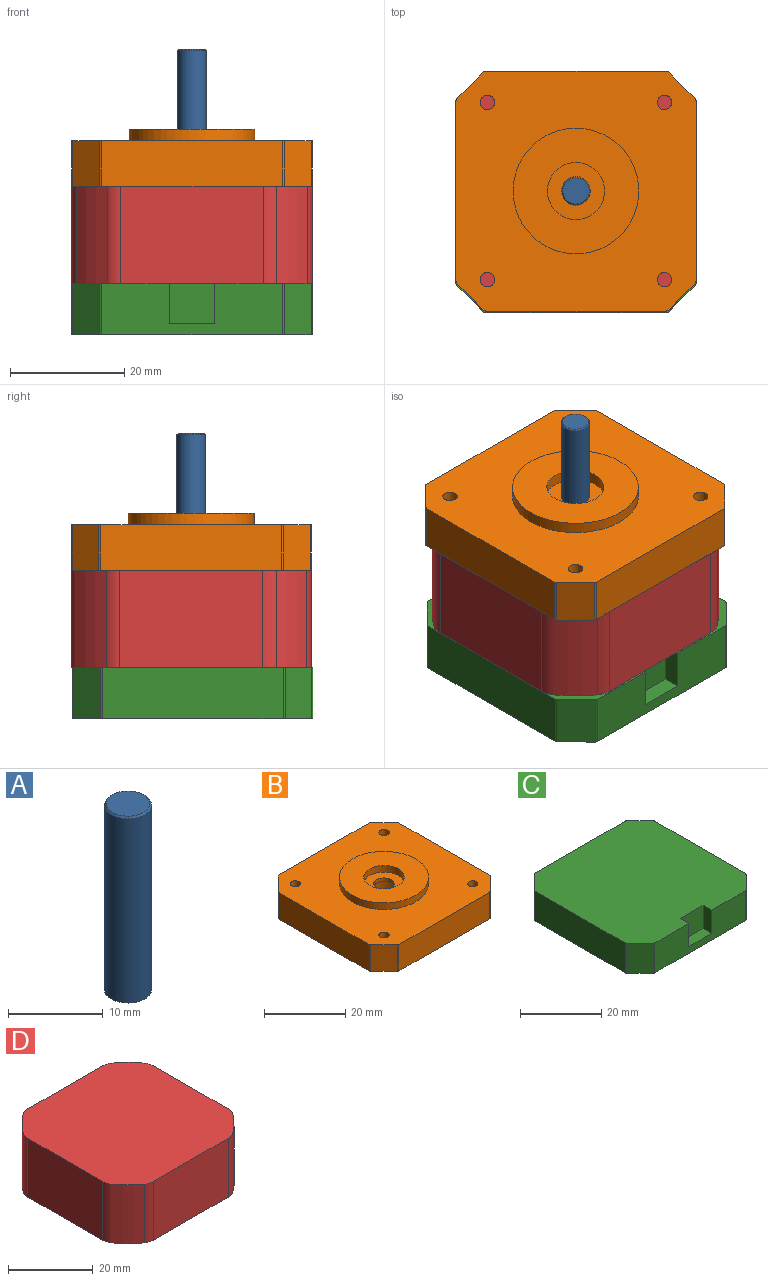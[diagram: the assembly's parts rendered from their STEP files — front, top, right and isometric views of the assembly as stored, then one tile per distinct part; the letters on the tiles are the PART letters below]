
ASSEMBLY  parts=4 mates=3
PART A: 4 faces, bbox 5x5x24 mm
  f0: cone r=2.4mm half-angle=45deg, axis (0,0,-1), area 4.3mm2, adj f1,f2
  f1: cylinder r=2.5mm len=23.8mm, axis (0,0,1), area 373.8mm2, adj f0,f3
  f2: plane 4.6x4.6mm, normal (0,0,1), area 16.6mm2, adj f0
  f3: plane 5x5mm, normal (0,0,-1), area 19.6mm2, adj f1
PART B: 29 faces, bbox 42x42x10 mm
  f0: cylinder r=0.5mm len=8mm, axis (0,0,-1), area 3.1mm2, adj f1,f2,f22,f25
  f1: plane 42x42mm, normal (0,0,1), area 1313.7mm2, adj f0,f2,f3,f4,f5,f6,f7,f8
  f2: plane 8x4.71mm, normal (-0.71,0.71,0), area 53.3mm2, adj f0,f1,f3,f25
  f3: cylinder r=0.5mm len=8mm, axis (0,0,-1), area 3.1mm2, adj f1,f2,f23,f25
  f4: cylinder r=0.5mm len=8mm, axis (0,0,-1), area 3.1mm2, adj f1,f5,f23,f25
  f5: plane 8x4.71mm, normal (-0.71,-0.71,0), area 53.3mm2, adj f1,f4,f6,f25
  f6: cylinder r=0.5mm len=8mm, axis (0,0,-1), area 3.1mm2, adj f1,f5,f24,f25
  f7: cylinder r=0.5mm len=8mm, axis (0,0,-1), area 3.1mm2, adj f1,f8,f24,f25
  f8: plane 8x4.71mm, normal (0.71,-0.71,0), area 53.3mm2, adj f1,f7,f9,f25
  f9: cylinder r=0.5mm len=8mm, axis (0,0,-1), area 3.1mm2, adj f1,f8,f21,f25
  f10: cylinder r=0.5mm len=8mm, axis (0,0,-1), area 3.1mm2, adj f1,f11,f21,f25
  f11: plane 8x4.71mm, normal (0.71,0.71,0), area 53.3mm2, adj f1,f10,f12,f25
  f12: cylinder r=0.5mm len=8mm, axis (0,0,-1), area 3.1mm2, adj f1,f11,f22,f25
  f13: cylinder r=2.5mm len=5mm, axis (0,0,-1), area 15.7mm2, adj f14,f15
  f14: plane 10x10mm, normal (0,0,1), area 58.9mm2, adj f13,f26
  f15: plane 10x10mm, normal (0,0,-1), area 58.9mm2, adj f13,f16
  f16: cylinder r=5mm len=10mm, axis (0,0,1), area 219.9mm2, adj f15,f25
  f17: cylinder r=1.26mm len=8mm, axis (0,0,-1), area 63.6mm2, adj f1,f25
  f18: cylinder r=1.26mm len=8mm, axis (0,0,-1), area 63.6mm2, adj f1,f25
  f19: cylinder r=1.26mm len=8mm, axis (0,0,-1), area 63.6mm2, adj f1,f25
  f20: cylinder r=1.26mm len=8mm, axis (0,0,-1), area 63.6mm2, adj f1,f25
  f21: plane 31.59x8mm, normal (1,0,0), area 252.7mm2, adj f1,f9,f10,f25
  f22: plane 31.59x8mm, normal (0,1,0), area 252.7mm2, adj f0,f1,f12,f25
  f23: plane 31.59x8mm, normal (-1,0,0), area 252.7mm2, adj f1,f3,f4,f25
  f24: plane 31.59x8mm, normal (0,-1,0), area 252.7mm2, adj f1,f6,f7,f25
  f25: plane 42x42mm, normal (0,0,-1), area 1615.3mm2, adj f0,f2,f3,f4,f5,f6,f7,f8
  f26: cylinder r=5mm len=10mm, axis (0,0,1), area 62.8mm2, adj f14,f28
  f27: cylinder r=11mm len=22mm, axis (0,0,1), area 138.2mm2, adj f1,f28
  f28: plane 22x22mm, normal (0,0,1), area 301.6mm2, adj f26,f27
PART C: 32 faces, bbox 42x42x9 mm
  f0: plane 7x3mm, normal (-1,0,0), area 21mm2, adj f2,f3,f4,f29
  f1: plane 7x3mm, normal (1,0,0), area 21mm2, adj f2,f3,f4,f29
  f2: plane 8x3mm, normal (0,0,1), area 24mm2, adj f0,f1,f3,f29
  f3: plane 8x7mm, normal (0,-1,0), area 56mm2, adj f0,f1,f2,f4
  f4: plane 42x42mm, normal (0,0,1), area 1690mm2, adj f0,f1,f3,f5,f7,f8,f9,f10
  f5: cylinder r=0.5mm len=9mm, axis (0,0,1), area 3.5mm2, adj f4,f6,f7,f30
  f6: plane 42x42mm, normal (0,0,-1), area 1530mm2, adj f5,f7,f8,f9,f10,f11,f12,f13
  f7: plane 9x4.71mm, normal (-0.71,0.71,0), area 59.9mm2, adj f4,f5,f6,f8
  f8: cylinder r=0.5mm len=9mm, axis (0,0,1), area 3.5mm2, adj f4,f6,f7,f31
  f9: cylinder r=0.5mm len=9mm, axis (0,0,1), area 3.5mm2, adj f4,f6,f10,f29
  f10: plane 9x4.71mm, normal (-0.71,-0.71,0), area 59.9mm2, adj f4,f6,f9,f11
  f11: cylinder r=0.5mm len=9mm, axis (0,0,1), area 3.5mm2, adj f4,f6,f10,f30
  f12: cylinder r=0.5mm len=9mm, axis (0,0,1), area 3.5mm2, adj f4,f6,f13,f29
  f13: plane 9x4.71mm, normal (0.71,-0.71,0), area 59.9mm2, adj f4,f6,f12,f14
  f14: cylinder r=0.5mm len=9mm, axis (0,0,1), area 3.5mm2, adj f4,f6,f13,f15
  f15: plane 31.59x9mm, normal (1,0,0), area 284.3mm2, adj f4,f6,f14,f16
  f16: cylinder r=0.5mm len=9mm, axis (0,0,1), area 3.5mm2, adj f4,f6,f15,f17
  f17: plane 9x4.71mm, normal (0.71,0.71,0), area 59.9mm2, adj f4,f6,f16,f18
  f18: cylinder r=0.5mm len=9mm, axis (0,0,1), area 3.5mm2, adj f4,f6,f17,f31
  f19: cylinder r=4.75mm len=9.5mm, axis (0,0,1), area 104.5mm2, adj f6,f20
  f20: plane 9.5x9.5mm, normal (0,0,-1), area 70.9mm2, adj f19
  f21: cylinder r=3mm len=6mm, axis (0,0,1), area 56.5mm2, adj f6,f22
  f22: plane 6x6mm, normal (0,0,-1), area 28.3mm2, adj f21
  f23: cylinder r=3mm len=6mm, axis (0,0,1), area 56.5mm2, adj f6,f24
  f24: plane 6x6mm, normal (0,0,-1), area 28.3mm2, adj f23
  f25: cylinder r=3mm len=6mm, axis (0,0,1), area 56.5mm2, adj f6,f26
  f26: plane 6x6mm, normal (0,0,-1), area 28.3mm2, adj f25
  f27: cylinder r=3mm len=6mm, axis (0,0,1), area 56.5mm2, adj f6,f28
  f28: plane 6x6mm, normal (0,0,-1), area 28.3mm2, adj f27
  f29: plane 31.59x9mm, normal (0,-1,0), area 228.3mm2, adj f0,f1,f2,f4,f6,f9,f12
  f30: plane 31.59x9mm, normal (-1,0,0), area 284.3mm2, adj f4,f5,f6,f11
  f31: plane 31.59x9mm, normal (0,1,0), area 284.3mm2, adj f4,f6,f8,f18
PART D: 18 faces, bbox 42x42x17 mm
  f0: plane 25x17mm, normal (-1,0,0), area 424.9mm2, adj f1,f15,f16,f17
  f1: cylinder r=4mm len=17mm, axis (0,0,-1), area 43.1mm2, adj f0,f2,f16,f17
  f2: cylinder r=25.1mm len=17mm, axis (0,0,-1), area 129.2mm2, adj f1,f3,f16,f17
  f3: cylinder r=4mm len=17mm, axis (0,0,-1), area 43.1mm2, adj f2,f4,f16,f17
  f4: plane 25x17mm, normal (0,-1,0), area 424.9mm2, adj f3,f5,f16,f17
  f5: cylinder r=4mm len=17mm, axis (0,0,-1), area 43.1mm2, adj f4,f6,f16,f17
  f6: cylinder r=25.1mm len=17mm, axis (0,0,-1), area 129.2mm2, adj f5,f7,f16,f17
  f7: cylinder r=4mm len=17mm, axis (0,0,-1), area 43.1mm2, adj f6,f8,f16,f17
  f8: plane 25x17mm, normal (1,0,0), area 424.9mm2, adj f7,f9,f16,f17
  f9: cylinder r=4mm len=17mm, axis (0,0,-1), area 43.1mm2, adj f8,f10,f16,f17
  f10: cylinder r=25.1mm len=17mm, axis (0,0,-1), area 129.2mm2, adj f9,f11,f16,f17
  f11: cylinder r=4mm len=17mm, axis (0,0,-1), area 43.1mm2, adj f10,f12,f16,f17
  f12: plane 25x17mm, normal (0,1,0), area 424.9mm2, adj f11,f13,f16,f17
  f13: cylinder r=4mm len=17mm, axis (0,0,-1), area 43.1mm2, adj f12,f14,f16,f17
  f14: cylinder r=25.1mm len=17mm, axis (0,0,-1), area 129.2mm2, adj f13,f15,f16,f17
  f15: cylinder r=4mm len=17mm, axis (0,0,-1), area 43.1mm2, adj f0,f14,f16,f17
  f16: plane 42x42mm, normal (0,0,-1), area 1672mm2, adj f0,f1,f2,f3,f4,f5,f6,f7
  f17: plane 42x42mm, normal (0,0,1), area 1672mm2, adj f0,f1,f2,f3,f4,f5,f6,f7
PLACE A t=(0,0.28,26)mm
PLACE B t=(0,0.28,34)mm
PLACE C t=(0,0,34)mm
PLACE D t=(0,0.28,34)mm
MATE fastened B.f13 <-> D.f2  axis (0,0,1) through (0,0.28,26)mm
MATE fastened A.f0 <-> D.f2  axis (0,0,-1) through (0,0.28,26)mm
MATE fastened D.f2 <-> C.f4  axis (0,0,-1) through (0,0.28,9)mm
